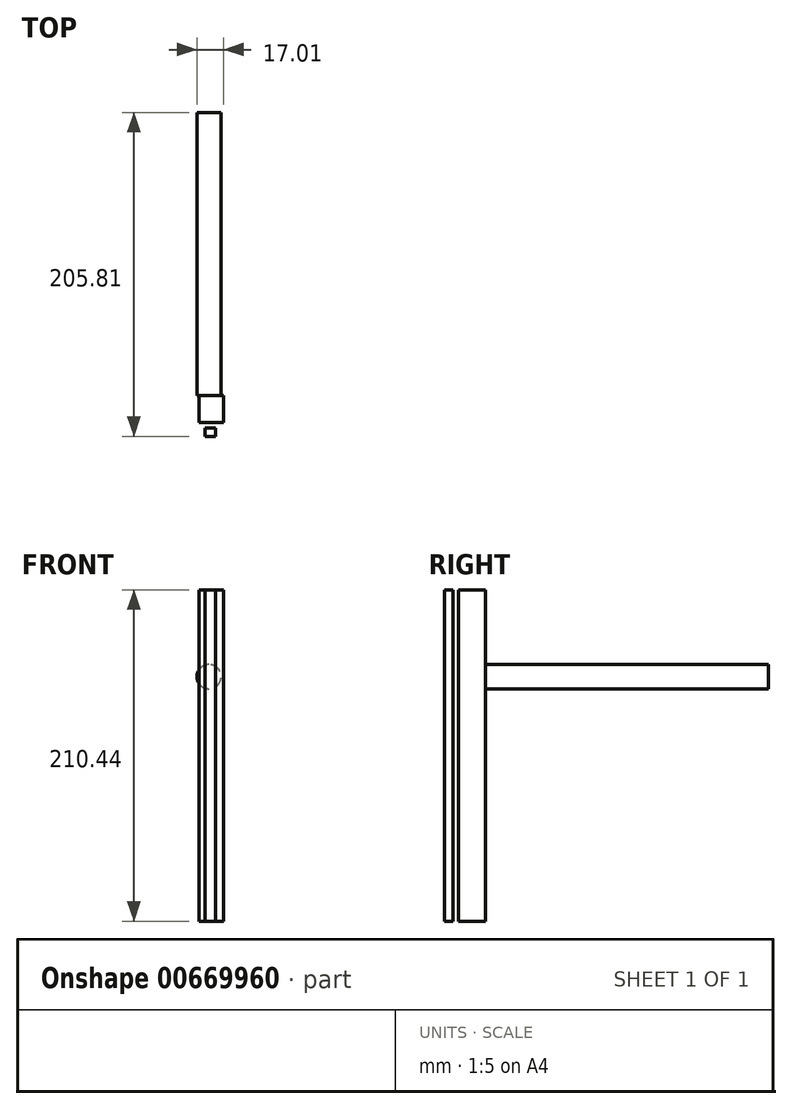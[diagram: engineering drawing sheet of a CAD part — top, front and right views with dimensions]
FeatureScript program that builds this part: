
annotation { "Feature Type Name" : "Feature", "Feature Type Description" : "" }
export const myFeature = defineFeature(function(context is Context, id is Id, definition is map)
    precondition{}
    {
        {
            var Q0;
            Q0=qCreatedBy(makeId("Top.planeOp"),FACE);
            var sketch = newSketch(context, id + "F0", { "sketchPlane" : qUnion([Q0])});
            skLineSegment(sketch, "E0.bottom", {"start": v(27.56, 8.96) * mm, "end": v(11.82, 8.96) * mm});
            skLineSegment(sketch, "E0.top", {"start": v(27.56, 26.05) * mm, "end": v(11.82, 26.05) * mm});
            skLineSegment(sketch, "E0.left", {"start": v(27.56, 8.96) * mm, "end": v(27.56, 26.05) * mm});
            skLineSegment(sketch, "E0.right", {"start": v(11.82, 8.96) * mm, "end": v(11.82, 26.05) * mm});
            skLineSegment(sketch, "E1.bottom", {"start": v(22.58, 0) * mm, "end": v(15.6, 0) * mm});
            skLineSegment(sketch, "E1.top", {"start": v(22.58, 5.29) * mm, "end": v(15.6, 5.29) * mm});
            skLineSegment(sketch, "E1.left", {"start": v(22.58, 0) * mm, "end": v(22.58, 5.29) * mm});
            skLineSegment(sketch, "E1.right", {"start": v(15.6, 0) * mm, "end": v(15.6, 5.29) * mm});
            skSolve(sketch);
        }
        {
            var Q0;
            Q0=makeQuery(id+"F0.imprint","IMPRINT",FACE,{"disambiguationData":[TD([[makeQuery(id+"F0.imprint","IMPRINT",EDGE,{"derivedFrom":sQuery(id+"F0.wireOp",EDGE,"E0.bottom")}),-1.0]])]});
            var Q1;
            Q1 = qSketchRegion(id + "F0", true);
            extrude(context, id + "F1", {"entities" : qUnion([Q0, Q1]), "depth" : 210.44 * mm, "offsetDistance" : 25 * mm});
        }
        {
            var Q0;
            Q0=makeQuery(id+"F1.opExtrude","SWEPT_FACE",FACE,{"disambiguationData":[OSD([sQuery(id+"F0.wireOp",EDGE,"E0.top")])]});
            var sketch = newSketch(context, id + "F2", { "sketchPlane" : qUnion([Q0])});
            skCircle(sketch, "E2", {"center": v(-18.26, 155.33) * mm, "radius": 7.71 * mm});
            skSolve(sketch);
        }
        {
            var Q0;
            Q0 = qSketchRegion(id + "F2", true);
            extrude(context, id + "F3", {"entities" : qUnion([Q0]), "operationType" : NewBodyOperationType.ADD, "depth" : 179.76 * mm, "offsetDistance" : 25 * mm});
        }
    });
